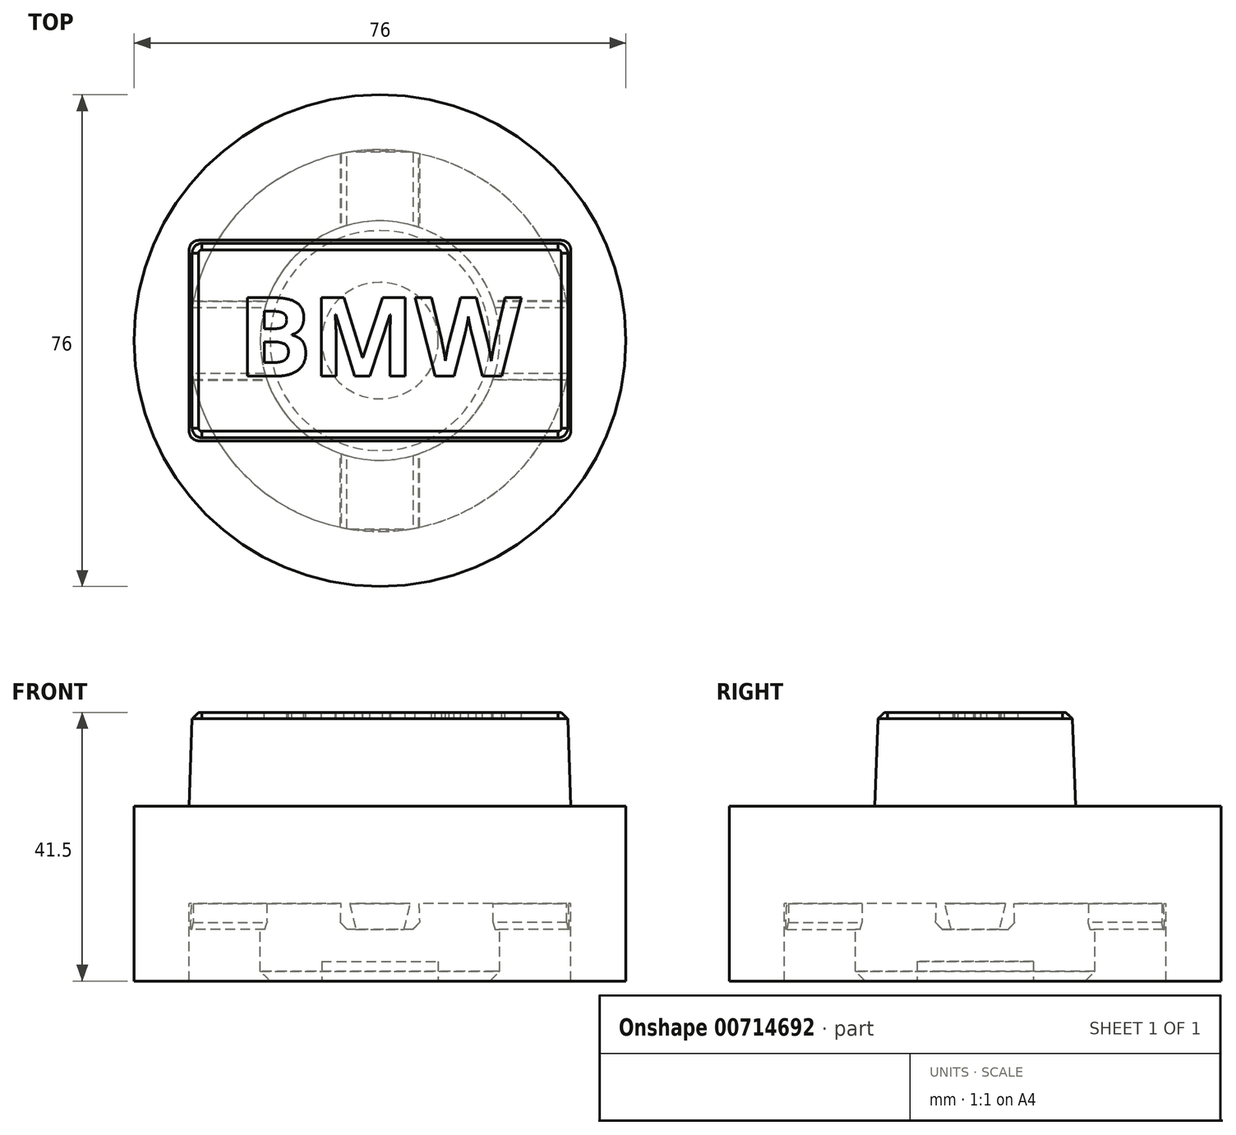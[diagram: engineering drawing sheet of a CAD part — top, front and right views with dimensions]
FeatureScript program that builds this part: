
annotation { "Feature Type Name" : "Feature", "Feature Type Description" : "" }
export const myFeature = defineFeature(function(context is Context, id is Id, definition is map)
    precondition{}
    {
        {
            var Q0;
            Q0=qCreatedBy(makeId("Top.planeOp"),FACE);
            var sketch = newSketch(context, id + "F0", { "sketchPlane" : qUnion([Q0])});
            skCircle(sketch, "E0", {"center": v(0, 0) * mm, "radius": 38 * mm});
            skSolve(sketch);
        }
        {
            var Q0;
            Q0 = qSketchRegion(id + "F0", true);
            extrude(context, id + "F1", {"entities" : qUnion([Q0]), "depth" : 15 * mm, "offsetDistance" : 25 * mm});
        }
        {
            var Q0;
            Q0=makeQuery(id+"F1.opExtrude","CAP_FACE",FACE,{"disambiguationData":[OSD([sQuery(id+"F0.wireOp",EDGE,"E0")])],"isStart":true});
            var sketch = newSketch(context, id + "F2", { "sketchPlane" : qUnion([Q0])});
            skCircle(sketch, "E1", {"center": v(0, 0) * mm, "radius": 18.5 * mm});
            skCircle(sketch, "E2", {"center": v(0, 0) * mm, "radius": 29.5 * mm});
            skSolve(sketch);
        }
        {
            var Q0;
            Q0=makeQuery(id+"F2.imprint","IMPRINT",FACE,{"disambiguationData":[TD([[makeQuery(id+"F2.imprint","IMPRINT",EDGE,{"derivedFrom":sQuery(id+"F2.wireOp",EDGE,"E2")}),-1.0]])]});
            var Q1;
            Q1=makeQuery(id+"F2.imprint","IMPRINT",FACE,{"disambiguationData":[TD([[makeQuery(id+"F2.imprint","IMPRINT",EDGE,{"derivedFrom":sQuery(id+"F2.wireOp",EDGE,"E1")}),1.0]])]});
            extrude(context, id + "F3", {"entities" : qUnion([Q0, Q1]), "operationType" : NewBodyOperationType.ADD, "depth" : 12 * mm, "offsetDistance" : 25 * mm});
        }
        {
            var Q0;
            Q0=makeQuery(id+"F1.opExtrude","CAP_FACE",FACE,{"disambiguationData":[OSD([sQuery(id+"F0.wireOp",EDGE,"E0")])],"isStart":false});
            var sketch = newSketch(context, id + "F4", { "sketchPlane" : qUnion([Q0])});
            skLineSegment(sketch, "E3.bottom", {"start": v(29.5, 15.5) * mm, "end": v(-29.5, 15.5) * mm});
            skLineSegment(sketch, "E3.top", {"start": v(29.5, -15.5) * mm, "end": v(-29.5, -15.5) * mm});
            skLineSegment(sketch, "E3.left", {"start": v(29.5, 15.5) * mm, "end": v(29.5, -15.5) * mm});
            skLineSegment(sketch, "E3.right", {"start": v(-29.5, 15.5) * mm, "end": v(-29.5, -15.5) * mm});
            skLineSegment(sketch, "E4", {"start": v(0, 0) * mm, "end": v(29.5, 0) * mm, "construction": true});
            skLineSegment(sketch, "E5", {"start": v(0, 0) * mm, "end": v(0, -15.5) * mm, "construction": true});
            skSolve(sketch);
        }
        {
            var Q0;
            Q0 = qSketchRegion(id + "F4", true);
            extrude(context, id + "F5", {"entities" : qUnion([Q0]), "operationType" : NewBodyOperationType.ADD, "depth" : 14.5 * mm, "offsetDistance" : 25 * mm, "hasDraft" : true, "draftAngle" : 2 * degree, "draftPullDirection" : true});
        }
        {
            var Q0;
            Q0=makeQuery(id+"F5.opExtrude","SWEPT_EDGE",EDGE,{"disambiguationData":[OSD([sQuery(id+"F4.wireOp",EDGE,"E3.top"),sQuery(id+"F4.wireOp",EDGE,"E3.right")])]});
            var Q1;
            Q1=makeQuery(id+"F5.opExtrude","SWEPT_EDGE",EDGE,{"disambiguationData":[OSD([sQuery(id+"F4.wireOp",EDGE,"E3.bottom"),sQuery(id+"F4.wireOp",EDGE,"E3.right")])]});
            var Q2;
            Q2=makeQuery(id+"F5.opExtrude","SWEPT_EDGE",EDGE,{"disambiguationData":[OSD([sQuery(id+"F4.wireOp",EDGE,"E3.top"),sQuery(id+"F4.wireOp",EDGE,"E3.left")])]});
            var Q3;
            Q3=makeQuery(id+"F5.opExtrude","SWEPT_EDGE",EDGE,{"disambiguationData":[OSD([sQuery(id+"F4.wireOp",EDGE,"E3.bottom"),sQuery(id+"F4.wireOp",EDGE,"E3.left")])]});
            fillet(context, id + "F6", {"entities" : qUnion([Q0, Q1, Q2, Q3]), "radius" : 1.5 * mm, "tangentPropagation" : true, "allowEdgeOverflow" : false});
        }
        {
            var Q0;
            Q0=makeQuery(id+"F5.opExtrude","CAP_EDGE",EDGE,{"disambiguationData":[OSD([sQuery(id+"F4.wireOp",EDGE,"E3.top")])],"isStart":false});
            chamfer(context, id + "F7", {"entities" : qUnion([Q0]), "width" : 1 * mm, "tangentPropagation" : true});
        }
        {
            var Q0;
            Q0=makeQuery(id+"F5.opExtrude","CAP_FACE",FACE,{"disambiguationData":[OSD([sQuery(id+"F4.wireOp",EDGE,"E3.bottom"),sQuery(id+"F4.wireOp",EDGE,"E3.top"),sQuery(id+"F4.wireOp",EDGE,"E3.left"),sQuery(id+"F4.wireOp",EDGE,"E3.right")])],"isStart":false});
            var sketch = newSketch(context, id + "F8", { "sketchPlane" : qUnion([Q0])});
            skText(sketch, "E6", { "text": "BMW", "fontName": "NotoSans-Bold.ttf"});
            const initialGuessF8  = {"E6": [-0.022, -0.0055, 1, 0, 0.01224]};
            skSetInitialGuess(sketch, initialGuessF8);
            skSolve(sketch);
        }
        {
            var Q0;
            Q0 = qSketchRegion(id + "F8", true);
            extrude(context, id + "F9", {"entities" : qUnion([Q0]), "operationType" : NewBodyOperationType.REMOVE, "oppositeDirection" : true, "depth" : 1 * mm, "offsetDistance" : 25 * mm});
        }
        {
            var Q0;
            Q0=makeQuery(id+"F3.opExtrude","CAP_FACE",FACE,{"disambiguationData":[OSD([sQuery(id+"F2.wireOp",EDGE,"E1")])],"isStart":false});
            var sketch = newSketch(context, id + "F10", { "sketchPlane" : qUnion([Q0])});
            skCircle(sketch, "E7", {"center": v(0, 0) * mm, "radius": 9 * mm});
            skSolve(sketch);
        }
        {
            var Q0;
            Q0 = qSketchRegion(id + "F10", true);
            extrude(context, id + "F11", {"entities" : qUnion([Q0]), "operationType" : NewBodyOperationType.REMOVE, "oppositeDirection" : true, "depth" : 3 * mm, "offsetDistance" : 25 * mm});
        }
        {
            var Q0;
            Q0=makeQuery(id+"F3.opExtrude","CAP_EDGE",EDGE,{"disambiguationData":[OSD([sQuery(id+"F2.wireOp",EDGE,"E1")])],"isStart":false});
            chamfer(context, id + "F12", {"entities" : qUnion([Q0]), "width" : 1.5 * mm, "tangentPropagation" : true});
        }
        {
            var Q0;
            Q0=makeQuery(id+"F1.opExtrude","CAP_FACE",FACE,{"disambiguationData":[OSD([sQuery(id+"F0.wireOp",EDGE,"E0")])],"isStart":true});
            var sketch = newSketch(context, id + "F13", { "sketchPlane" : qUnion([Q0])});
            skLineSegment(sketch, "E8", {"start": v(0, 13.73) * mm, "end": v(0, 30.47) * mm, "construction": true});
            skLineSegment(sketch, "E9.bottom", {"start": v(-6, 29.13) * mm, "end": v(6, 29.13) * mm});
            skLineSegment(sketch, "E9.top", {"start": v(-6, 15.07) * mm, "end": v(6, 15.07) * mm});
            skLineSegment(sketch, "E9.left", {"start": v(-6, 29.13) * mm, "end": v(-6, 15.07) * mm});
            skLineSegment(sketch, "E9.right", {"start": v(6, 29.13) * mm, "end": v(6, 15.07) * mm});
            skLineSegment(sketch, "E10", {"start": v(0, 22.1) * mm, "end": v(6, 22.1) * mm});
            skLineSegment(sketch, "E11", {"start": v(0, 22.1) * mm, "end": v(0, 29.13) * mm});
            skLineSegment(sketch, "E12.1.0", {"start": v(-29.13, -6) * mm, "end": v(-15.07, -6) * mm});
            skLineSegment(sketch, "E12.1.1", {"start": v(-29.13, -6) * mm, "end": v(-29.13, 6) * mm});
            skLineSegment(sketch, "E12.1.2", {"start": v(-29.13, 6) * mm, "end": v(-15.07, 6) * mm});
            skLineSegment(sketch, "E12.1.3", {"start": v(-15.07, -6) * mm, "end": v(-15.07, 6) * mm});
            skLineSegment(sketch, "E12.2.0", {"start": v(6, -29.13) * mm, "end": v(6, -15.07) * mm});
            skLineSegment(sketch, "E12.2.1", {"start": v(6, -29.13) * mm, "end": v(-6, -29.13) * mm});
            skLineSegment(sketch, "E12.2.2", {"start": v(-6, -29.13) * mm, "end": v(-6, -15.07) * mm});
            skLineSegment(sketch, "E12.2.3", {"start": v(6, -15.07) * mm, "end": v(-6, -15.07) * mm});
            skLineSegment(sketch, "E12.3.0", {"start": v(29.13, 6) * mm, "end": v(15.07, 6) * mm});
            skLineSegment(sketch, "E12.3.1", {"start": v(29.13, 6) * mm, "end": v(29.13, -6) * mm});
            skLineSegment(sketch, "E12.3.2", {"start": v(29.13, -6) * mm, "end": v(15.07, -6) * mm});
            skLineSegment(sketch, "E12.3.3", {"start": v(15.07, 6) * mm, "end": v(15.07, -6) * mm});
            skPoint(sketch, "E12.center", {"position": v(0, 0) * mm});
            skSolve(sketch);
        }
        {
            var Q0;
            Q0 = qSketchRegion(id + "F13", true);
            extrude(context, id + "F14", {"entities" : qUnion([Q0]), "operationType" : NewBodyOperationType.ADD, "depth" : 4 * mm, "offsetDistance" : 25 * mm, "hasDraft" : true, "draftAngle" : 2 * degree});
        }
        {
            var Q0;
            Q0=makeQuery(id+"F14.opExtrude","CAP_EDGE",EDGE,{"disambiguationData":[OSD([sQuery(id+"F13.wireOp",EDGE,"E9.left")])],"isStart":false});
            var Q1;
            Q1=makeQuery(id+"F14.opExtrude","CAP_EDGE",EDGE,{"disambiguationData":[OSD([sQuery(id+"F13.wireOp",EDGE,"E9.right")])],"isStart":false});
            var Q2;
            Q2=makeQuery(id+"F14.opExtrude","CAP_EDGE",EDGE,{"disambiguationData":[OSD([sQuery(id+"F13.wireOp",EDGE,"E12.3.0")])],"isStart":false});
            var Q3;
            Q3=makeQuery(id+"F14.opExtrude","CAP_EDGE",EDGE,{"disambiguationData":[OSD([sQuery(id+"F13.wireOp",EDGE,"E12.3.2")])],"isStart":false});
            var Q4;
            Q4=makeQuery(id+"F14.opExtrude","CAP_EDGE",EDGE,{"disambiguationData":[OSD([sQuery(id+"F13.wireOp",EDGE,"E12.2.0")])],"isStart":false});
            var Q5;
            Q5=makeQuery(id+"F14.opExtrude","CAP_EDGE",EDGE,{"disambiguationData":[OSD([sQuery(id+"F13.wireOp",EDGE,"E12.2.2")])],"isStart":false});
            var Q6;
            Q6=makeQuery(id+"F14.opExtrude","CAP_EDGE",EDGE,{"disambiguationData":[OSD([sQuery(id+"F13.wireOp",EDGE,"E12.1.0")])],"isStart":false});
            var Q7;
            Q7=makeQuery(id+"F14.opExtrude","CAP_EDGE",EDGE,{"disambiguationData":[OSD([sQuery(id+"F13.wireOp",EDGE,"E12.1.2")])],"isStart":false});
            chamfer(context, id + "F15", {"entities" : qUnion([Q0, Q1, Q2, Q3, Q4, Q5, Q6, Q7]), "width" : 1 * mm, "tangentPropagation" : true});
        }
    });
